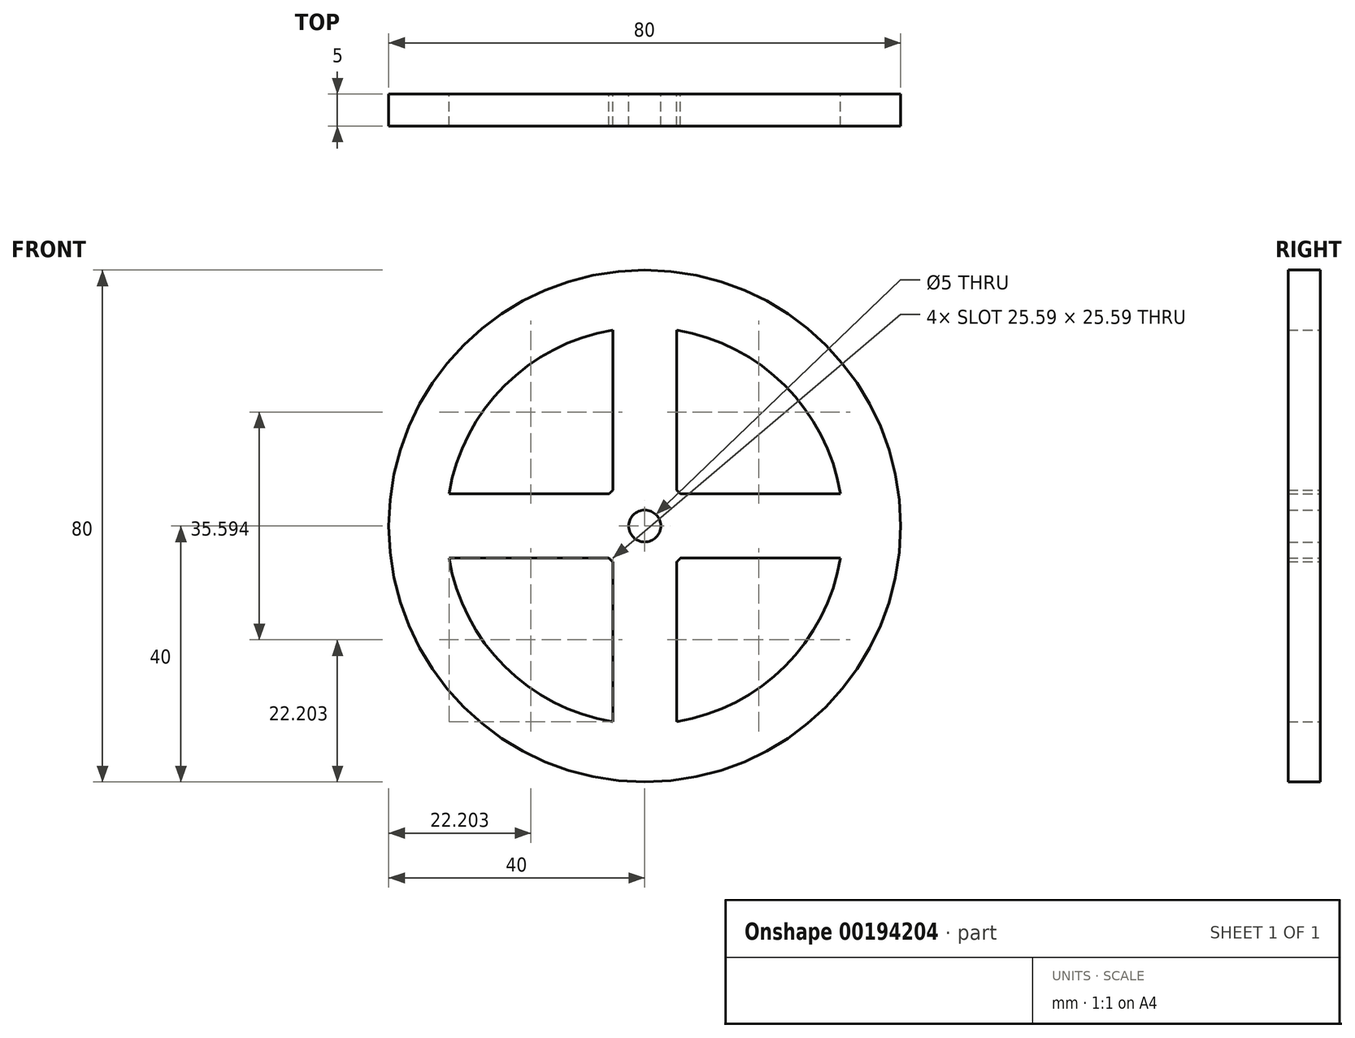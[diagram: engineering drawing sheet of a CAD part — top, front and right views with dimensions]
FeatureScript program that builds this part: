
annotation { "Feature Type Name" : "Feature", "Feature Type Description" : "" }
export const myFeature = defineFeature(function(context is Context, id is Id, definition is map)
    precondition{}
    {
        {
            var Q0;
            Q0=qCreatedBy(makeId("Front.planeOp"),FACE);
            var sketch = newSketch(context, id + "F0", { "sketchPlane" : qUnion([Q0])});
            skCircle(sketch, "E0", {"center": v(0, 0) * mm, "radius": 2.5 * mm});
            skArc(sketch, "E1", {"start": v(-5, 5.6) * mm, "mid": v(-5.3, 5.3) * mm, "end": v(-5.6, 5) * mm});
            skArc(sketch, "E2", {"start": v(5, -30.6) * mm, "mid": v(21.92, -21.92) * mm, "end": v(30.6, -5) * mm});
            skCircle(sketch, "E3", {"center": v(0, 0) * mm, "radius": 40 * mm});
            skLineSegment(sketch, "E4", {"start": v(0, 0) * mm, "end": v(0, 31) * mm, "construction": true});
            skLineSegment(sketch, "E5", {"start": v(0, 0) * mm, "end": v(31, 0) * mm, "construction": true});
            skLineSegment(sketch, "E6", {"start": v(0, 0) * mm, "end": v(-31, 0) * mm, "construction": true});
            skLineSegment(sketch, "E7", {"start": v(0, 0) * mm, "end": v(0, -31) * mm, "construction": true});
            skLineSegment(sketch, "E8.0", {"start": v(5, 5.6) * mm, "end": v(5, 30.6) * mm});
            skLineSegment(sketch, "E9.0", {"start": v(-5, 5.6) * mm, "end": v(-5, 30.6) * mm});
            skLineSegment(sketch, "E10.0", {"start": v(5.6, -5) * mm, "end": v(30.6, -5) * mm});
            skLineSegment(sketch, "E11.0", {"start": v(5.6, 5) * mm, "end": v(30.6, 5) * mm});
            skLineSegment(sketch, "E12.0", {"start": v(-5, -5.6) * mm, "end": v(-5, -30.6) * mm});
            skLineSegment(sketch, "E13.0", {"start": v(5, -5.6) * mm, "end": v(5, -30.6) * mm});
            skLineSegment(sketch, "E14.0", {"start": v(-5.6, 5) * mm, "end": v(-30.6, 5) * mm});
            skLineSegment(sketch, "E15.0", {"start": v(-5.6, -5) * mm, "end": v(-30.6, -5) * mm});
            skArc(sketch, "E16.trimOffspring", {"start": v(5.6, 5) * mm, "mid": v(5.3, 5.3) * mm, "end": v(5, 5.6) * mm});
            skArc(sketch, "E17.trimOffspring", {"start": v(5, -5.6) * mm, "mid": v(5.3, -5.3) * mm, "end": v(5.6, -5) * mm});
            skArc(sketch, "E18.trimOffspring", {"start": v(-5.6, -5) * mm, "mid": v(-5.3, -5.3) * mm, "end": v(-5, -5.6) * mm});
            skArc(sketch, "E19.trimOffspring", {"start": v(30.6, 5) * mm, "mid": v(21.92, 21.92) * mm, "end": v(5, 30.6) * mm});
            skArc(sketch, "E20.trimOffspring", {"start": v(-30.6, -5) * mm, "mid": v(-21.92, -21.92) * mm, "end": v(-5, -30.6) * mm});
            skArc(sketch, "E21.trimOffspring", {"start": v(-5, 30.6) * mm, "mid": v(-21.92, 21.92) * mm, "end": v(-30.6, 5) * mm});
            skSolve(sketch);
        }
        {
            var Q0;
            Q0=makeQuery(id+"F0.imprint","IMPRINT",FACE,{"disambiguationData":[TD([[makeQuery(id+"F0.imprint","IMPRINT",EDGE,{"derivedFrom":sQuery(id+"F0.wireOp",EDGE,"E0")}),-1.0]])]});
            extrude(context, id + "F1", {"entities" : qUnion([Q0]), "endBound" : BoundingType.SYMMETRIC, "depth" : 5 * mm});
        }
    });
